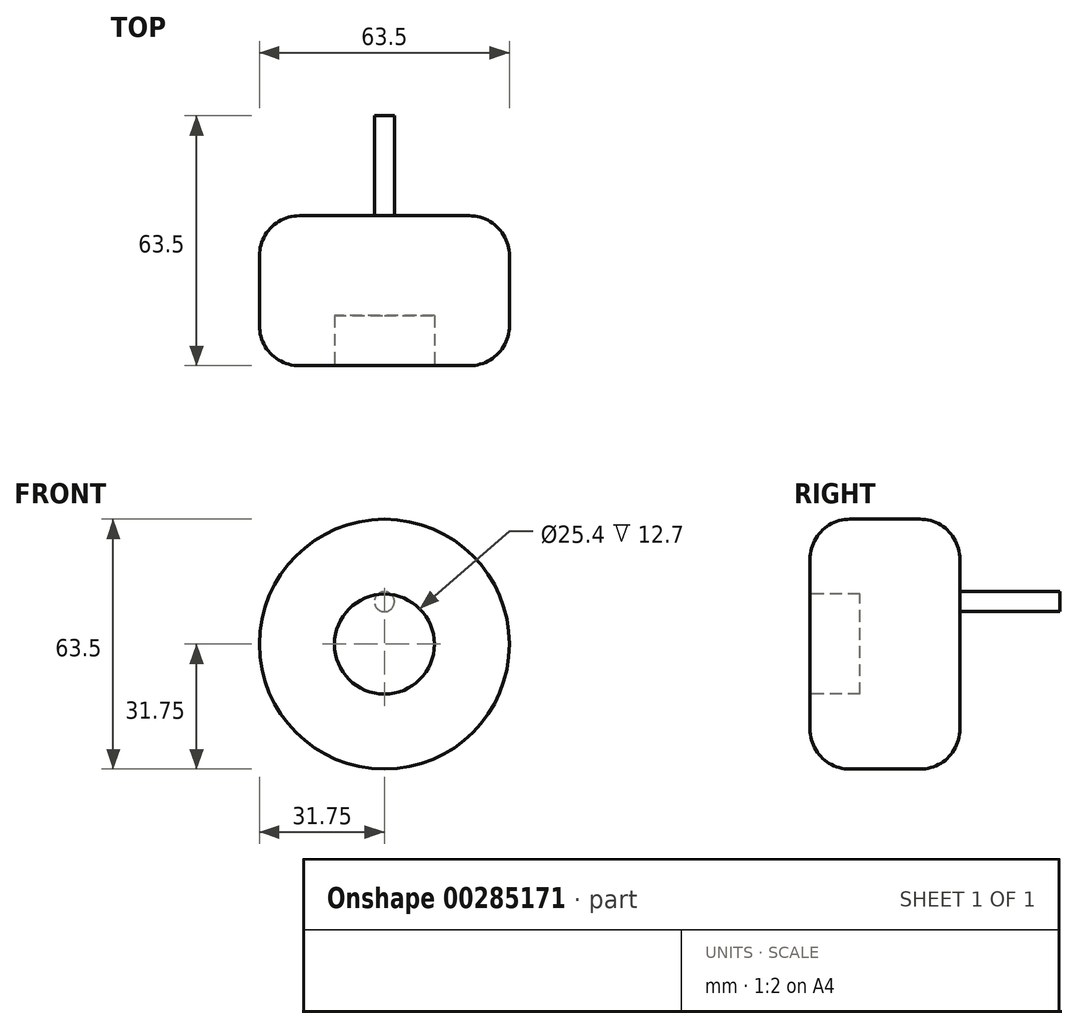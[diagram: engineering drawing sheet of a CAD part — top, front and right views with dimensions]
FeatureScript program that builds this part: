
annotation { "Feature Type Name" : "Feature", "Feature Type Description" : "" }
export const myFeature = defineFeature(function(context is Context, id is Id, definition is map)
    precondition{}
    {
        {
            var Q0;
            Q0=qCreatedBy(makeId("Front.planeOp"),FACE);
            var sketch = newSketch(context, id + "F0", { "sketchPlane" : qUnion([Q0])});
            skCircle(sketch, "E0", {"center": v(0, 0) * mm, "radius": 31.75 * mm});
            skSolve(sketch);
        }
        {
            var Q0;
            Q0=makeQuery(id+"F0.imprint","IMPRINT",FACE,{"disambiguationData":[TD([[makeQuery(id+"F0.imprint","IMPRINT",EDGE,{"derivedFrom":sQuery(id+"F0.wireOp",EDGE,"E0")}),1.0]])]});
            extrude(context, id + "F1", {"entities" : qUnion([Q0]), "depth" : 38.1 * mm});
        }
        {
            var Q0;
            Q0=makeQuery(id+"F1.opExtrude","CAP_EDGE",EDGE,{"disambiguationData":[OSD([sQuery(id+"F0.wireOp",EDGE,"E0")])],"isStart":false});
            var Q1;
            Q1=makeQuery(id+"F1.opExtrude","CAP_EDGE",EDGE,{"disambiguationData":[OSD([sQuery(id+"F0.wireOp",EDGE,"E0")])],"isStart":true});
            fillet(context, id + "F2", {"entities" : qUnion([Q0, Q1]), "radius" : 10.16 * mm, "tangentPropagation" : true, "allowEdgeOverflow" : false});
        }
        {
            var Q0;
            Q0=makeQuery(id+"F1.opExtrude","CAP_FACE",FACE,{"disambiguationData":[OSD([sQuery(id+"F0.wireOp",EDGE,"E0")])],"isStart":false});
            var sketch = newSketch(context, id + "F3", { "sketchPlane" : qUnion([Q0])});
            skCircle(sketch, "E1", {"center": v(0, 0) * mm, "radius": 12.7 * mm});
            skSolve(sketch);
        }
        {
            var Q0;
            Q0=makeQuery(id+"F3.imprint","IMPRINT",FACE,{"disambiguationData":[TD([[makeQuery(id+"F3.imprint","IMPRINT",EDGE,{"derivedFrom":sQuery(id+"F3.wireOp",EDGE,"E1")}),1.0]])]});
            extrude(context, id + "F4", {"entities" : qUnion([Q0]), "operationType" : NewBodyOperationType.REMOVE, "oppositeDirection" : true, "depth" : 12.7 * mm});
        }
        {
            var Q0;
            Q0=makeQuery(id+"F1.opExtrude","CAP_FACE",FACE,{"disambiguationData":[OSD([sQuery(id+"F0.wireOp",EDGE,"E0")])],"isStart":true});
            var sketch = newSketch(context, id + "F5", { "sketchPlane" : qUnion([Q0])});
            skLineSegment(sketch, "E2", {"start": v(0, 0) * mm, "end": v(0, 21.59) * mm, "construction": true});
            skCircle(sketch, "E3", {"center": v(0, 10.8) * mm, "radius": 2.54 * mm});
            skSolve(sketch);
        }
        {
            var Q0;
            Q0=makeQuery(id+"F5.imprint","IMPRINT",FACE,{"disambiguationData":[TD([[makeQuery(id+"F5.imprint","IMPRINT",EDGE,{"derivedFrom":sQuery(id+"F5.wireOp",EDGE,"E3")}),1.0]])]});
            extrude(context, id + "F6", {"entities" : qUnion([Q0]), "operationType" : NewBodyOperationType.ADD, "depth" : 25.4 * mm});
        }
    });
